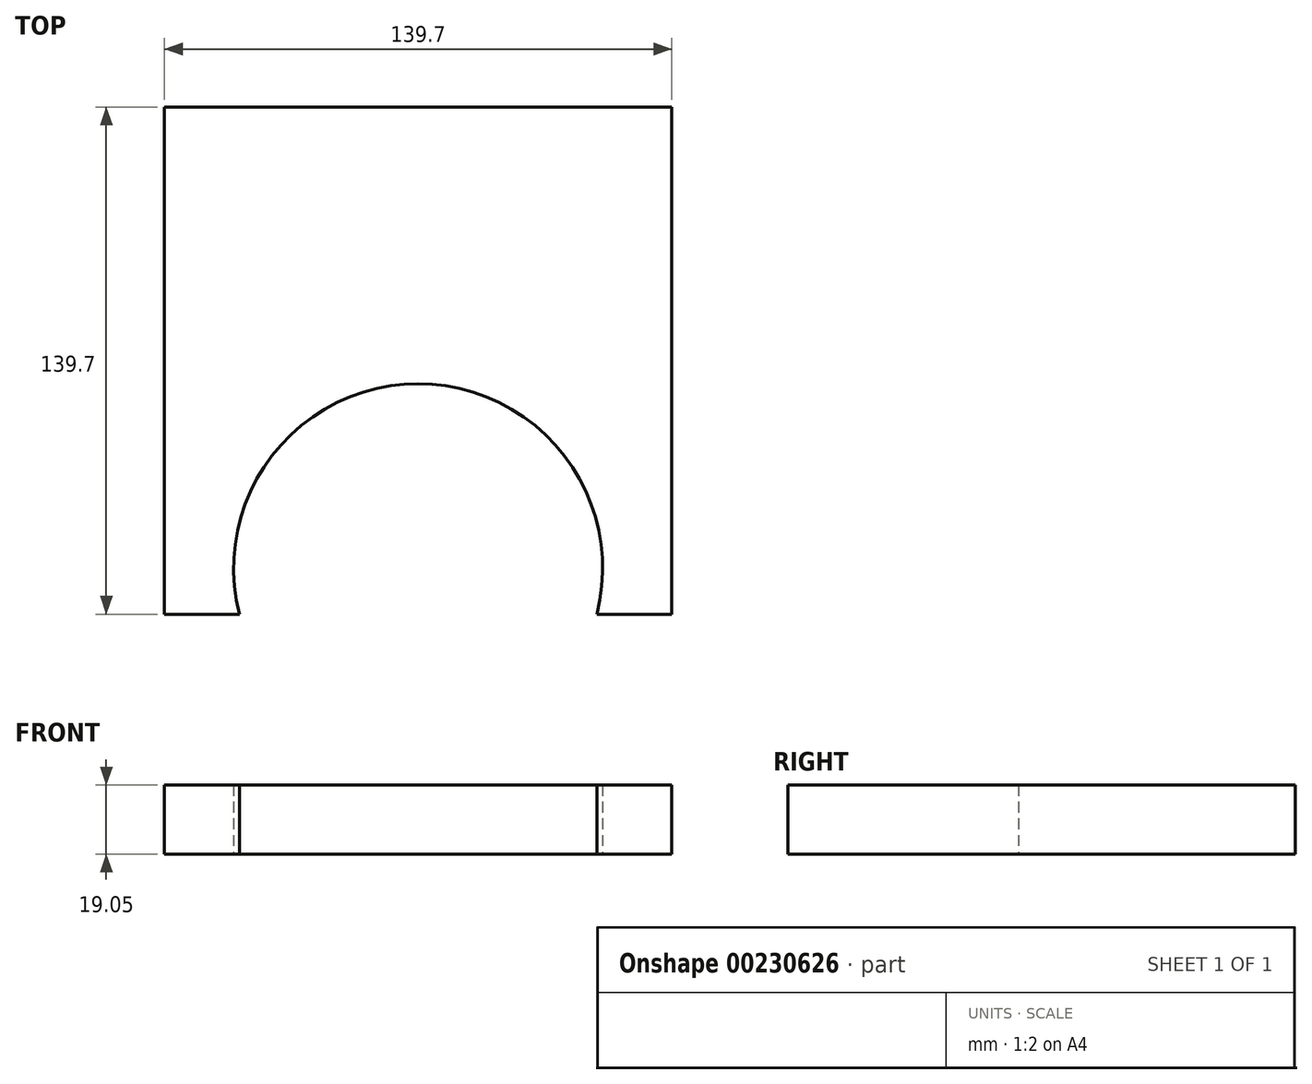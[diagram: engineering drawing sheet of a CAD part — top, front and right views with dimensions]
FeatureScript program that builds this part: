
annotation { "Feature Type Name" : "Feature", "Feature Type Description" : "" }
export const myFeature = defineFeature(function(context is Context, id is Id, definition is map)
    precondition{}
    {
        {
            var Q0;
            Q0=qCreatedBy(makeId("Top.planeOp"),FACE);
            var sketch = newSketch(context, id + "F0", { "sketchPlane" : qUnion([Q0])});
            skLineSegment(sketch, "E0.bottom", {"start": v(69.85, 69.85) * mm, "end": v(-69.85, 69.85) * mm});
            skLineSegment(sketch, "E0.top", {"start": v(69.85, -69.85) * mm, "end": v(49.19, -69.85) * mm});
            skLineSegment(sketch, "E0.left", {"start": v(69.85, 69.85) * mm, "end": v(69.85, -69.85) * mm});
            skLineSegment(sketch, "E0.right", {"start": v(-69.85, 69.85) * mm, "end": v(-69.85, -69.85) * mm});
            skPoint(sketch, "E0.middle", {"position": v(0, 0) * mm});
            skLineSegment(sketch, "E1", {"start": v(0, -69.85) * mm, "end": v(0, -57.15) * mm});
            skArc(sketch, "E2", {"start": v(49.19, -69.85) * mm, "mid": v(0, -6.35) * mm, "end": v(-49.19, -69.85) * mm});
            skLineSegment(sketch, "E3.trimOffspring", {"start": v(-49.19, -69.85) * mm, "end": v(-69.85, -69.85) * mm});
            skSolve(sketch);
        }
        {
            var Q0;
            Q0=makeQuery(id+"F0.imprint","IMPRINT",FACE,{"disambiguationData":[TD([[makeQuery(id+"F0.imprint","IMPRINT",EDGE,{"derivedFrom":sQuery(id+"F0.wireOp",EDGE,"E0.bottom")}),1.0]])]});
            extrude(context, id + "F1", {"entities" : qUnion([Q0]), "depth" : 19.05 * mm});
        }
    });
